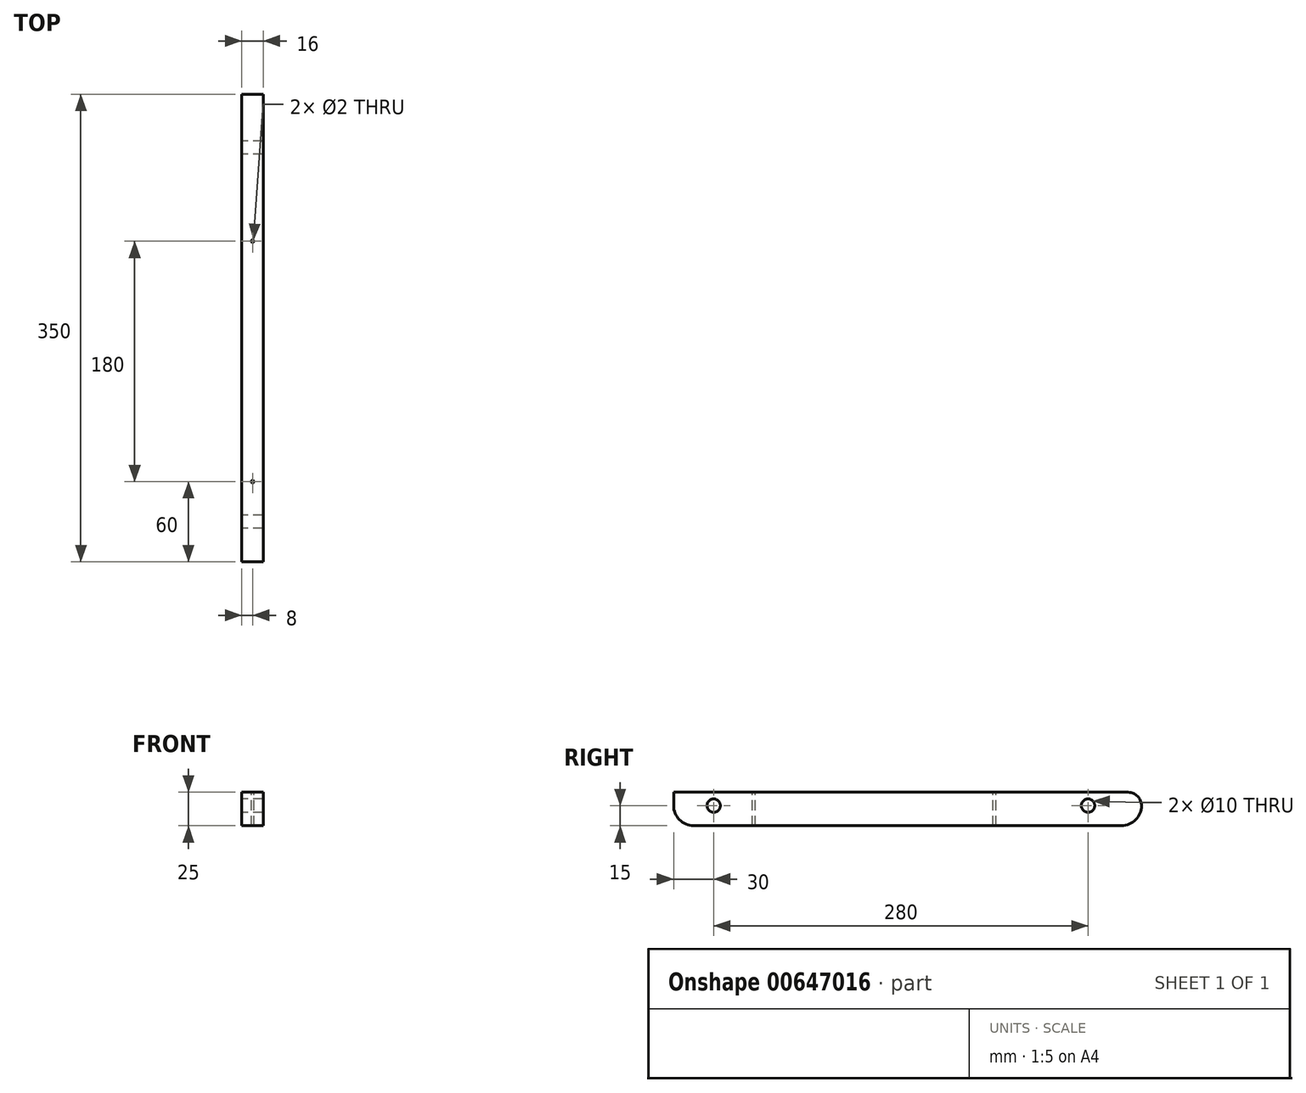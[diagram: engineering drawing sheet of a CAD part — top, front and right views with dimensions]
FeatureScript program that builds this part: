
annotation { "Feature Type Name" : "Feature", "Feature Type Description" : "" }
export const myFeature = defineFeature(function(context is Context, id is Id, definition is map)
    precondition{}
    {
        {
            var Q0;
            Q0=qCreatedBy(makeId("Right.planeOp"),FACE);
            var sketch = newSketch(context, id + "F0", { "sketchPlane" : qUnion([Q0])});
            skLineSegment(sketch, "E0.bottom", {"start": v(165, 0) * mm, "end": v(-175, 0) * mm});
            skLineSegment(sketch, "E0.top", {"start": v(160, -25) * mm, "end": v(-160, -25) * mm});
            skLineSegment(sketch, "E0.left", {"start": v(175, -10) * mm, "end": v(175, -10) * mm});
            skLineSegment(sketch, "E0.right", {"start": v(-175, 0) * mm, "end": v(-175, -10) * mm});
            skPoint(sketch, "E0.middle", {"position": v(0, -12.5) * mm});
            skPoint(sketch, "E1.visualSharp", {"position": v(-175, -25) * mm});
            skArc(sketch, "E1.filletArc", {"start": v(-175, -10) * mm, "mid": v(-170.6, -20.6) * mm, "end": v(-160, -25) * mm});
            skPoint(sketch, "E2.visualSharp", {"position": v(175, -25) * mm});
            skArc(sketch, "E2.filletArc", {"start": v(160, -25) * mm, "mid": v(170.6, -20.6) * mm, "end": v(175, -10) * mm});
            skLineSegment(sketch, "E3", {"start": v(-145, -10) * mm, "end": v(135, -10) * mm, "construction": true});
            skCircle(sketch, "E4", {"center": v(-145, -10) * mm, "radius": 5 * mm});
            skCircle(sketch, "E5", {"center": v(135, -10) * mm, "radius": 5 * mm});
            skPoint(sketch, "E6.visualSharp", {"position": v(175, 0) * mm});
            skArc(sketch, "E6.filletArc", {"start": v(175, -10) * mm, "mid": v(172.07, -2.93) * mm, "end": v(165, 0) * mm});
            skSolve(sketch);
        }
        {
            var Q0;
            Q0 = qSketchRegion(id + "F0", true);
            extrude(context, id + "F1", {"entities" : qUnion([Q0]), "endBound" : BoundingType.SYMMETRIC, "depth" : 16 * mm, "offsetDistance" : 25 * mm});
        }
        {
            var Q0;
            Q0=qCreatedBy(makeId("Top.planeOp"),FACE);
            var sketch = newSketch(context, id + "F2", { "sketchPlane" : qUnion([Q0])});
            skLineSegment(sketch, "E7", {"start": v(0, 65) * mm, "end": v(0, -115) * mm, "construction": true});
            skCircle(sketch, "E8", {"center": v(0, 65) * mm, "radius": 1 * mm});
            skCircle(sketch, "E9", {"center": v(0, -115) * mm, "radius": 1 * mm});
            skSolve(sketch);
        }
        {
            var Q0;
            Q0 = qSketchRegion(id + "F2", true);
            extrude(context, id + "F3", {"entities" : qUnion([Q0]), "operationType" : NewBodyOperationType.REMOVE, "endBound" : BoundingType.THROUGH_ALL, "oppositeDirection" : true, "depth" : 25 * mm, "offsetDistance" : 25 * mm});
        }
    });
